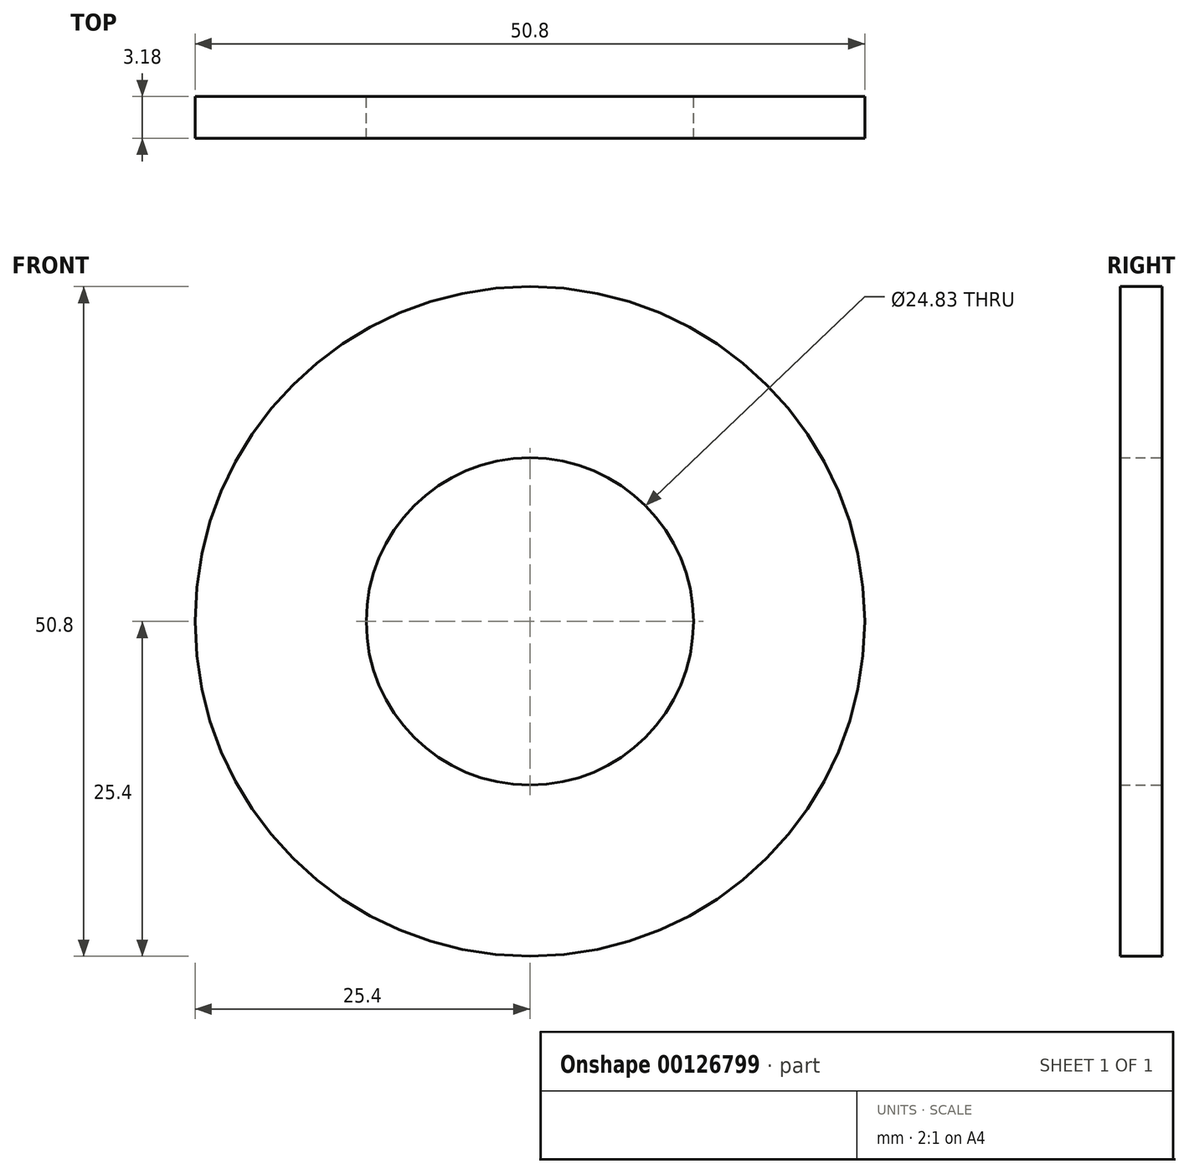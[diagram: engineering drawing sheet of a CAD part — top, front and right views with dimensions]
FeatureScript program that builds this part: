
annotation { "Feature Type Name" : "Feature", "Feature Type Description" : "" }
export const myFeature = defineFeature(function(context is Context, id is Id, definition is map)
    precondition{}
    {
        {
            var Q0;
            Q0=qCreatedBy(makeId("Front.planeOp"),FACE);
            var sketch = newSketch(context, id + "F0", { "sketchPlane" : qUnion([Q0])});
            skCircle(sketch, "E0", {"center": v(0, 0) * mm, "radius": 25.4 * mm});
            skCircle(sketch, "E1", {"center": v(0, 0) * mm, "radius": 12.41 * mm});
            skSolve(sketch);
        }
        {
            var Q0;
            Q0=makeQuery(id+"F0.imprint","IMPRINT",FACE,{"disambiguationData":[TD([[makeQuery(id+"F0.imprint","IMPRINT",EDGE,{"derivedFrom":sQuery(id+"F0.wireOp",EDGE,"E0")}),1.0]])]});
            extrude(context, id + "F1", {"entities" : qUnion([Q0]), "depth" : 3.17 * mm});
        }
    });
